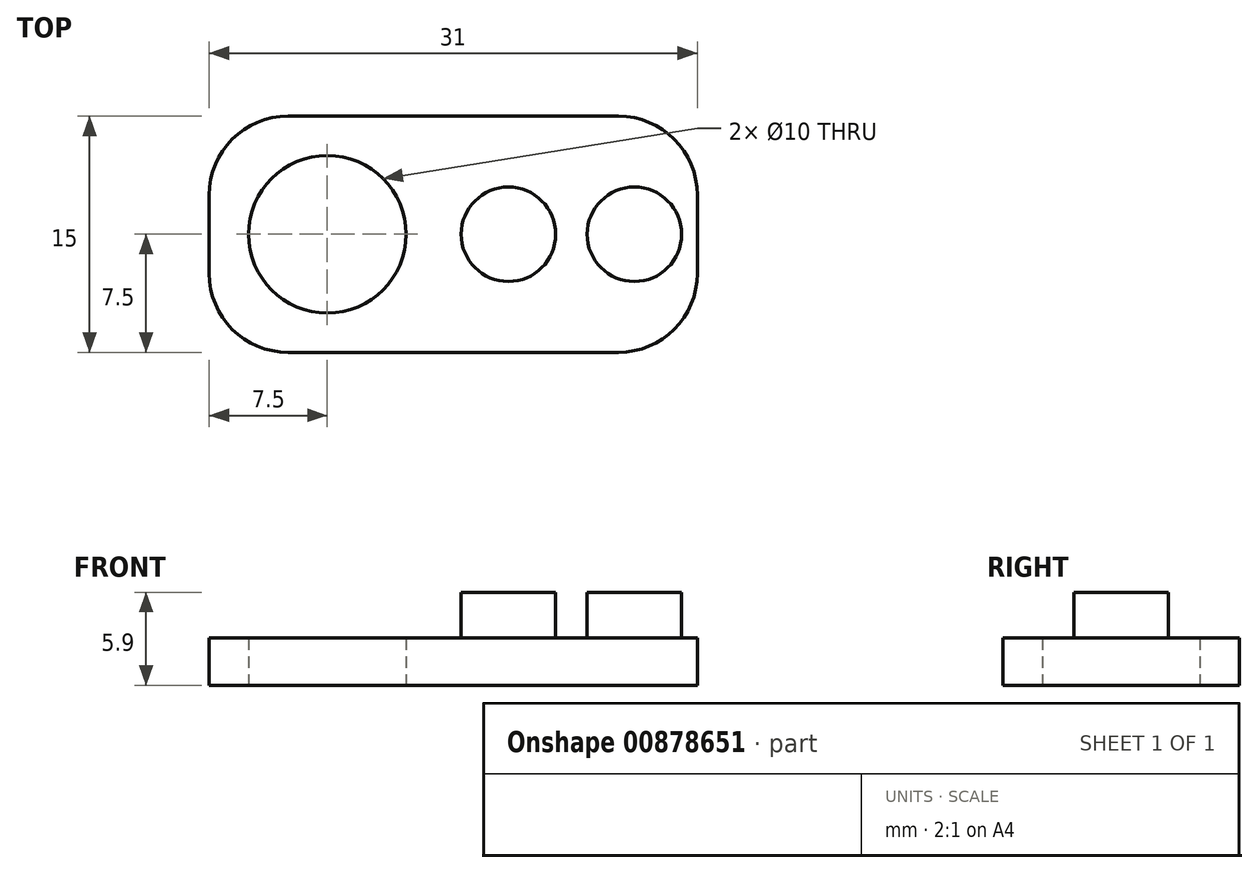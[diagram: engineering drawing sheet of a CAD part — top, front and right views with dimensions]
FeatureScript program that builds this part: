
annotation { "Feature Type Name" : "Feature", "Feature Type Description" : "" }
export const myFeature = defineFeature(function(context is Context, id is Id, definition is map)
    precondition{}
    {
        {
            var Q0;
            Q0=qCreatedBy(makeId("Top.planeOp"),FACE);
            var sketch = newSketch(context, id + "F0", { "sketchPlane" : qUnion([Q0])});
            skLineSegment(sketch, "E0.bottom", {"start": v(8, -7.5) * mm, "end": v(-8, -7.5) * mm});
            skLineSegment(sketch, "E0.top", {"start": v(8, 7.5) * mm, "end": v(-8, 7.5) * mm});
            skLineSegment(sketch, "E0.left", {"start": v(8, -7.5) * mm, "end": v(8, 7.5) * mm});
            skLineSegment(sketch, "E0.right", {"start": v(-8, -7.5) * mm, "end": v(-8, 7.5) * mm});
            skPoint(sketch, "E0.middle", {"position": v(0, 0) * mm});
            skLineSegment(sketch, "E1", {"start": v(0, 0) * mm, "end": v(4, 0) * mm});
            skCircle(sketch, "E2", {"center": v(4, 0) * mm, "radius": 3 * mm});
            skCircle(sketch, "E3", {"center": v(-4, 0) * mm, "radius": 3 * mm});
            skLineSegment(sketch, "E4.bottom", {"start": v(-8, 7.5) * mm, "end": v(-23, 7.5) * mm});
            skLineSegment(sketch, "E4.top", {"start": v(-8, -7.5) * mm, "end": v(-23, -7.5) * mm});
            skLineSegment(sketch, "E4.left", {"start": v(-8, 7.5) * mm, "end": v(-8, -7.5) * mm});
            skLineSegment(sketch, "E4.right", {"start": v(-23, 7.5) * mm, "end": v(-23, -7.5) * mm});
            skLineSegment(sketch, "E5", {"start": v(-23, 0) * mm, "end": v(-15.5, 0) * mm});
            skCircle(sketch, "E6", {"center": v(-15.5, 0) * mm, "radius": 5 * mm});
            skLineSegment(sketch, "E7", {"start": v(0, 0) * mm, "end": v(-4, 0) * mm});
            skSolve(sketch);
        }
        {
            var Q0;
            {var subQ1=sQuery(id+"F0.wireOp",EDGE,"E4.bottom");Q0=makeQuery(id+"F0.imprint","IMPRINT",FACE,{"disambiguationData":[TD([[makeQuery(id+"F0.imprint","IMPRINT",EDGE,{"derivedFrom":subQ1}),1.0]])]});}
            var Q1;
            Q1=makeQuery(id+"F0.imprint","IMPRINT",FACE,{"disambiguationData":[TD([[makeQuery(id+"F0.imprint","IMPRINT",EDGE,{"derivedFrom":sQuery(id+"F0.wireOp",EDGE,"E0.bottom")}),-1.0]])]});
            extrude(context, id + "F1", {"entities" : qUnion([Q0, Q1]), "flatOperationType" : FlatOperationType.REMOVE, "depth" : 3 * mm, "offsetDistance" : 25 * mm, "domain" : OperationDomain.MODEL});
        }
        {
            var Q0;
            Q0=makeQuery(id+"F0.imprint","IMPRINT",FACE,{"disambiguationData":[TD([[makeQuery(id+"F0.imprint","IMPRINT",EDGE,{"derivedFrom":sQuery(id+"F0.wireOp",EDGE,"E3")}),1.0]])]});
            var Q1;
            Q1=makeQuery(id+"F0.imprint","IMPRINT",FACE,{"disambiguationData":[TD([[makeQuery(id+"F0.imprint","IMPRINT",EDGE,{"derivedFrom":sQuery(id+"F0.wireOp",EDGE,"E2")}),1.0]])]});
            extrude(context, id + "F2", {"entities" : qUnion([Q0, Q1]), "operationType" : NewBodyOperationType.ADD, "flatOperationType" : FlatOperationType.REMOVE, "depth" : 5.9 * mm, "offsetDistance" : 25 * mm, "domain" : OperationDomain.MODEL});
        }
        {
            var Q0;
            Q0=makeQuery(id+"F1.opExtrude","SWEPT_EDGE",EDGE,{"disambiguationData":[OSD([sQuery(id+"F0.wireOp",EDGE,"E4.top"),sQuery(id+"F0.wireOp",EDGE,"E4.right")])]});
            var Q1;
            Q1=makeQuery(id+"F1.opExtrude","SWEPT_EDGE",EDGE,{"disambiguationData":[OSD([sQuery(id+"F0.wireOp",EDGE,"E0.bottom"),sQuery(id+"F0.wireOp",EDGE,"E0.left")])]});
            var Q2;
            Q2=makeQuery(id+"F1.opExtrude","SWEPT_EDGE",EDGE,{"disambiguationData":[OSD([sQuery(id+"F0.wireOp",EDGE,"E4.bottom"),sQuery(id+"F0.wireOp",EDGE,"E4.right")])]});
            var Q3;
            Q3=makeQuery(id+"F1.opExtrude","SWEPT_EDGE",EDGE,{"disambiguationData":[OSD([sQuery(id+"F0.wireOp",EDGE,"E0.top"),sQuery(id+"F0.wireOp",EDGE,"E0.left")])]});
            fillet(context, id + "F3", {"entities" : qUnion([Q0, Q1, Q2, Q3]), "radius" : 5 * mm, "tangentPropagation" : true, "defaultsChanged" : false, "vertexSettings" : [], "allowEdgeOverflow" : false});
        }
        {
            var Q0;
            Q0=makeQuery(id+"F1.opExtrude","SWEPT_BODY",BODY,{"disambiguationData":[OSD([sQuery(id+"F0.wireOp",EDGE,"E0.bottom"),sQuery(id+"F0.wireOp",EDGE,"E0.top"),sQuery(id+"F0.wireOp",EDGE,"E0.left"),sQuery(id+"F0.wireOp",EDGE,"E2"),sQuery(id+"F0.wireOp",EDGE,"E3"),sQuery(id+"F0.wireOp",EDGE,"E4.bottom"),sQuery(id+"F0.wireOp",EDGE,"E4.top"),sQuery(id+"F0.wireOp",EDGE,"E4.right"),sQuery(id+"F0.wireOp",EDGE,"E6")])]});
            transform(context, id + "F4", {"entities" : qUnion([Q0]), "transformType" : TransformType.TRANSLATION_3D, "dx" : 0 * mm, "dy" : 0 * mm, "dz" : 0 * mm, "makeCopy" : true});
        }
    });
